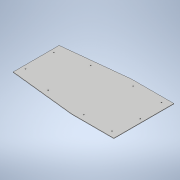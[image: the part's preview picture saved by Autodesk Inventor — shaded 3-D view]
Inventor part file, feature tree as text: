
AUTODESK INVENTOR PART (.ipt)
format: ipt  version: 2021 (Build 250183000, 183)  size: 138,240 bytes
history: native  units: in
note: dims shown in document units (in); Inventor stores cm internally (conversion verified against a paired STEP export)
features: extrude x1, sketch x1
ambient origin geometry x8: Origin, YZ Plane, XZ Plane, XY Plane, X Axis, Y Axis, Z Axis, Center Point
bodies: Solid1 (feature_tree)
feature tree (2):
  extrude  "Extrusion1"  Depth=1.0in
  sketch  "Sketch1"  dims[d0=8.5in d1=12.0in d2=30.5in d3=8.5in d4=12.0in d5=6.5in d6=6.5in d7=0.125in d8=0.0in d9=2.0in d10=1.5in d11=2.0in d12=1.5in d14=1.5in d15=4.0in d16=1.0in d17=4.0in d18=1.0in d19=0.25in d20=0.25in d21=1.5in d22=0.25in d23=2.0in d24=1.5in d25=2.0in d26=1.5in d27=0.25in d28=0.25in d29=0.25in d30=0.25in d31=0.25in d32=1.0in d33=0.25in]
